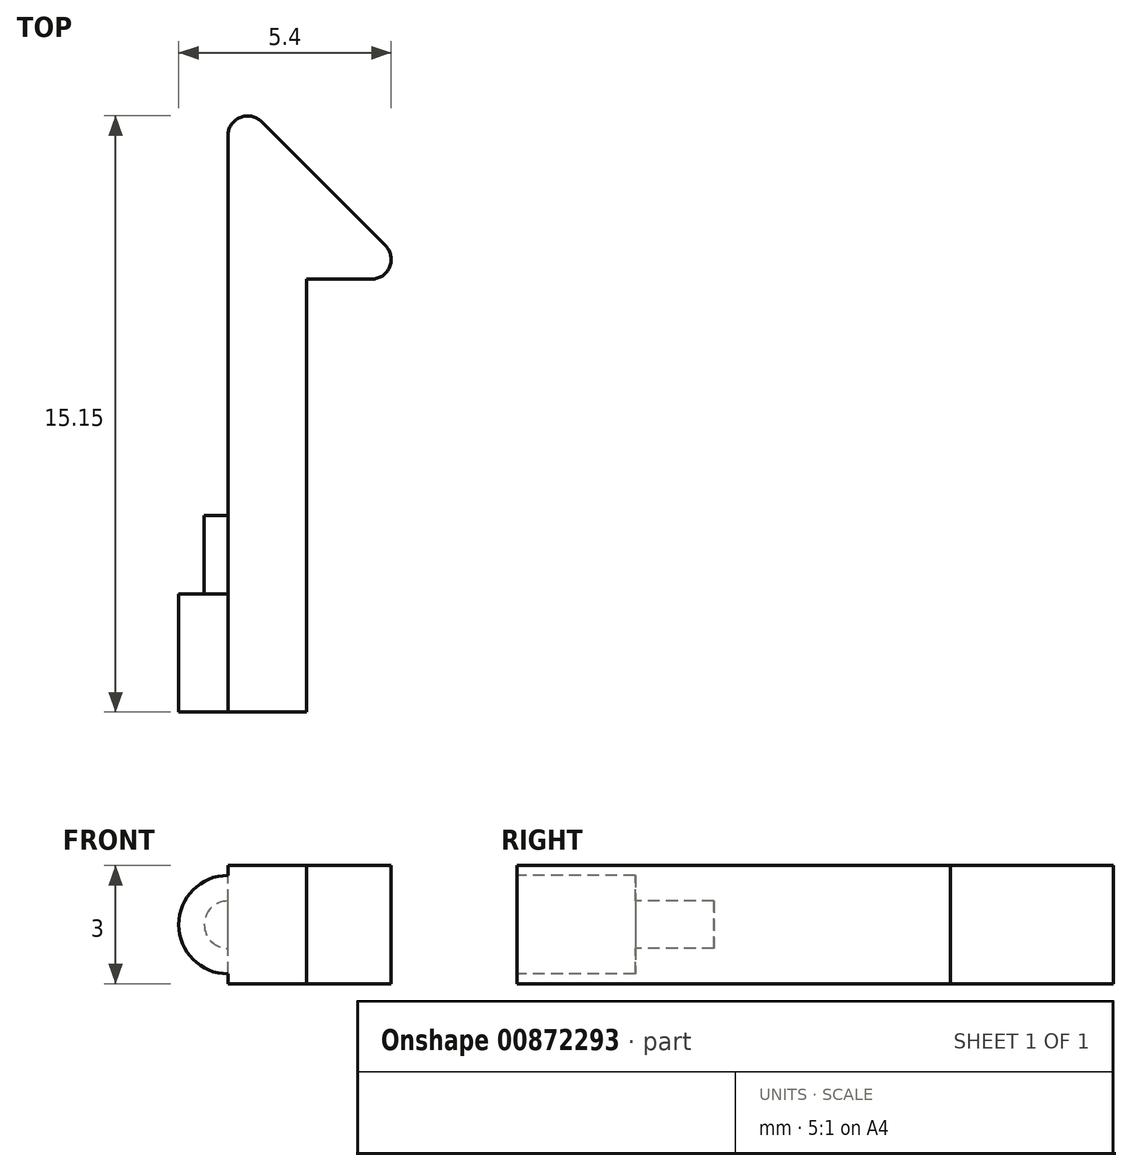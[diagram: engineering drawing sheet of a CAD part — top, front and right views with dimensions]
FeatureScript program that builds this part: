
annotation { "Feature Type Name" : "Feature", "Feature Type Description" : "" }
export const myFeature = defineFeature(function(context is Context, id is Id, definition is map)
    precondition{}
    {
        {
            var Q0;
            Q0=qCreatedBy(makeId("Top.planeOp"),FACE);
            var sketch = newSketch(context, id + "F0", { "sketchPlane" : qUnion([Q0])});
            skLineSegment(sketch, "E0.top", {"start": v(0, 0) * mm, "end": v(2, 0) * mm});
            skLineSegment(sketch, "E0.left", {"start": v(0, 14.65) * mm, "end": v(0, 0) * mm});
            skLineSegment(sketch, "E0.right", {"start": v(2, 11) * mm, "end": v(2, 0) * mm});
            skPoint(sketch, "E0.middle", {"position": v(0, 5.24) * mm});
            skLineSegment(sketch, "E1.top", {"start": v(2, 11) * mm, "end": v(3.65, 11) * mm});
            skLineSegment(sketch, "E1.left", {"start": v(0, 14.65) * mm, "end": v(0, 11) * mm});
            skLineSegment(sketch, "E2", {"start": v(0.85, 15) * mm, "end": v(4, 11.85) * mm});
            skArc(sketch, "E3.filletArc", {"start": v(0.85, 15) * mm, "mid": v(0.3, 15.1) * mm, "end": v(0, 14.65) * mm});
            skArc(sketch, "E4.filletArc", {"start": v(3.65, 11) * mm, "mid": v(4.1, 11.3) * mm, "end": v(4, 11.85) * mm});
            skSolve(sketch);
        }
        {
            var Q0;
            Q0=qCreatedBy(makeId("Front.planeOp"),FACE);
            var sketch = newSketch(context, id + "F1", { "sketchPlane" : qUnion([Q0])});
            skCircle(sketch, "E5", {"center": v(0, 0) * mm, "radius": 1.25 * mm});
            skCircle(sketch, "E6", {"center": v(0, 0) * mm, "radius": 0.6 * mm});
            skSolve(sketch);
        }
        {
            var Q0;
            Q0=makeQuery(id+"F0.imprint","IMPRINT",FACE,{"disambiguationData":[TD([[makeQuery(id+"F0.imprint","IMPRINT",EDGE,{"derivedFrom":sQuery(id+"F0.wireOp",EDGE,"E0.top")}),1.0]])]});
            extrude(context, id + "F2", {"entities" : qUnion([Q0]), "endBound" : BoundingType.SYMMETRIC, "oppositeDirection" : true, "depth" : 3 * mm, "offsetDistance" : 25 * mm});
        }
        {
            var Q0;
            Q0=makeQuery(id+"F1.imprint","IMPRINT",FACE,{"disambiguationData":[TD([[makeQuery(id+"F1.imprint","IMPRINT",EDGE,{"derivedFrom":sQuery(id+"F1.wireOp",EDGE,"E6")}),1.0]])]});
            extrude(context, id + "F3", {"entities" : qUnion([Q0]), "oppositeDirection" : true, "depth" : 5 * mm, "offsetDistance" : 25 * mm});
        }
        {
            var Q0;
            Q0 = qSketchRegion(id + "F1", true);
            extrude(context, id + "F4", {"entities" : qUnion([Q0]), "operationType" : NewBodyOperationType.ADD, "oppositeDirection" : true, "depth" : 3 * mm, "offsetDistance" : 25 * mm});
        }
    });
